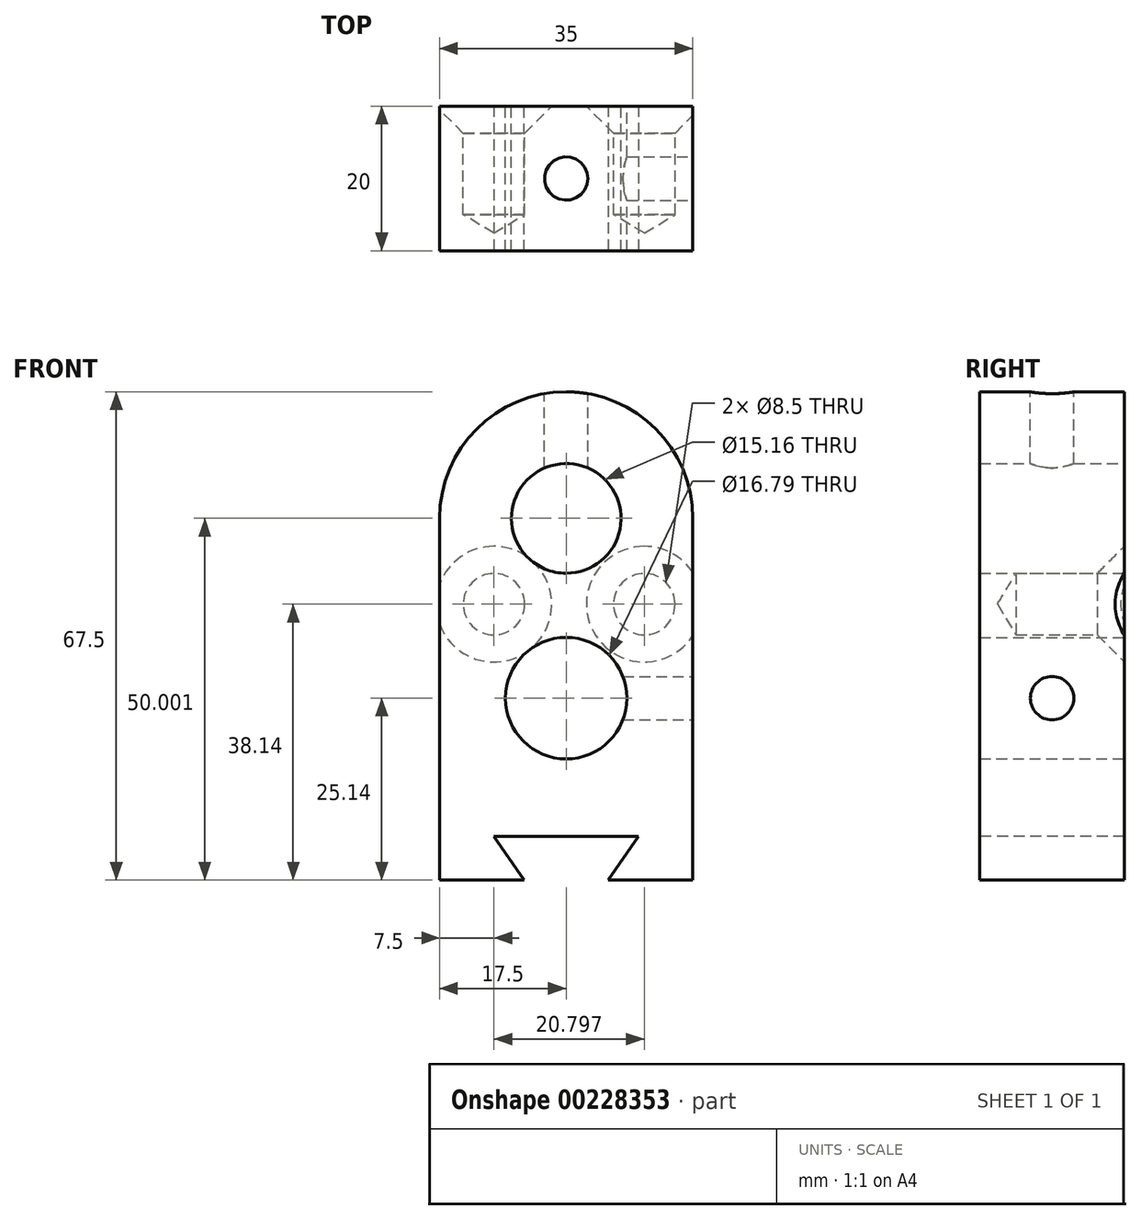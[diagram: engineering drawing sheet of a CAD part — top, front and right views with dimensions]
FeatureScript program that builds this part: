
annotation { "Feature Type Name" : "Feature", "Feature Type Description" : "" }
export const myFeature = defineFeature(function(context is Context, id is Id, definition is map)
    precondition{}
    {
        {
            var Q0;
            Q0=qCreatedBy(makeId("Front.planeOp"),FACE);
            var sketch = newSketch(context, id + "F0", { "sketchPlane" : qUnion([Q0])});
            skLineSegment(sketch, "E0.bottom", {"start": v(-17.5, -25.14) * mm, "end": v(17.5, -25.14) * mm});
            skLineSegment(sketch, "E0.left", {"start": v(-17.5, -25.14) * mm, "end": v(-17.5, 24.86) * mm});
            skLineSegment(sketch, "E0.right", {"start": v(17.5, -25.14) * mm, "end": v(17.5, 24.86) * mm});
            skArc(sketch, "E1", {"start": v(17.5, 24.86) * mm, "mid": v(0, 42.36) * mm, "end": v(-17.5, 24.86) * mm});
            skCircle(sketch, "E2", {"center": v(0, 24.86) * mm, "radius": 7.58 * mm});
            skCircle(sketch, "E3", {"center": v(0, 0) * mm, "radius": 8.4 * mm});
            skSolve(sketch);
        }
        {
            var Q0;
            Q0=makeQuery(id+"F0.imprint","IMPRINT",FACE,{"disambiguationData":[TD([[makeQuery(id+"F0.imprint","IMPRINT",EDGE,{"derivedFrom":sQuery(id+"F0.wireOp",EDGE,"E0.bottom")}),1.0]])]});
            extrude(context, id + "F1", {"entities" : qUnion([Q0]), "depth" : 20 * mm});
        }
        {
            var Q0;
            Q0=makeQuery(id+"F1.opExtrude","CAP_FACE",FACE,{"disambiguationData":[OSD([sQuery(id+"F0.wireOp",EDGE,"E0.bottom"),sQuery(id+"F0.wireOp",EDGE,"E0.left"),sQuery(id+"F0.wireOp",EDGE,"E0.right"),sQuery(id+"F0.wireOp",EDGE,"E1"),sQuery(id+"F0.wireOp",EDGE,"E2"),sQuery(id+"F0.wireOp",EDGE,"E3")])],"isStart":false});
            var sketch = newSketch(context, id + "F2", { "sketchPlane" : qUnion([Q0])});
            skLineSegment(sketch, "E4", {"start": v(0, -26.69) * mm, "end": v(0, -25.14) * mm, "construction": true});
            skLineSegment(sketch, "E5", {"start": v(8.93, -19.1) * mm, "end": v(7.4, -25.14) * mm});
            skLineSegment(sketch, "E6", {"start": v(7.4, -25.14) * mm, "end": v(-6.96, -25.14) * mm});
            skLineSegment(sketch, "E7", {"start": v(-6.96, -25.14) * mm, "end": v(-11.07, -26.69) * mm});
            skLineSegment(sketch, "E8", {"start": v(-11.07, -26.69) * mm, "end": v(8.93, -19.1) * mm});
            skSolve(sketch);
        }
        {
            var Q0;
            {var subQ3=sQuery(id+"F2.wireOp",EDGE,"E5");Q0=makeQuery(id+"F2.imprint","IMPRINT",FACE,{"disambiguationData":[TD([[makeQuery(id+"F2.imprint","IMPRINT",EDGE,{"derivedFrom":subQ3}),1.0]])]});}
            var sketch = newSketch(context, id + "F3", { "sketchPlane" : qUnion([Q0])});
            skLineSegment(sketch, "E9", {"start": v(-5.73, -25.24) * mm, "end": v(-10, -19.14) * mm});
            skLineSegment(sketch, "E10", {"start": v(-10, -19.14) * mm, "end": v(10, -19.14) * mm});
            skLineSegment(sketch, "E11", {"start": v(10, -19.14) * mm, "end": v(5.75, -25.2) * mm});
            skLineSegment(sketch, "E12", {"start": v(-5.73, -25.24) * mm, "end": v(5.75, -25.2) * mm});
            skSolve(sketch);
        }
        {
            var Q0;
            {var subQ0=sQuery(id+"F3.wireOp",EDGE,"E10");var subQ1=sQuery(id+"F3.wireOp",EDGE,"E9");var subQ2=makeQuery(id+"F3.imprint","INTERSECT",VERTEX,{"derivedFrom":[subQ1,subQ0]});Q0=makeQuery(id+"F3.imprint","IMPRINT",FACE,{"disambiguationData":[TD([[makeQuery(id+"F3.imprint","IMPRINT",EDGE,{"disambiguationData":[TD([[subQ2,1.0]])],"derivedFrom":subQ1}),-1.0]])]});}
            var Q1;
            {var subQ0=sQuery(id+"F3.wireOp",EDGE,"E12");Q1=makeQuery(id+"F3.imprint","IMPRINT",FACE,{"disambiguationData":[TD([[makeQuery(id+"F3.imprint","IMPRINT",EDGE,{"derivedFrom":subQ0}),1.0]])]});}
            var Q2;
            {var subQ0=sQuery(id+"F3.wireOp",EDGE,"E11");var subQ1=sQuery(id+"F3.wireOp",EDGE,"E10");var subQ2=makeQuery(id+"F3.imprint","INTERSECT",VERTEX,{"derivedFrom":[subQ1,subQ0]});Q2=makeQuery(id+"F3.imprint","IMPRINT",FACE,{"disambiguationData":[TD([[makeQuery(id+"F3.imprint","IMPRINT",EDGE,{"disambiguationData":[TD([[subQ2,1.0]])],"derivedFrom":subQ1}),-1.0]])]});}
            extrude(context, id + "F4", {"entities" : qUnion([Q0, Q1, Q2]), "operationType" : NewBodyOperationType.REMOVE, "oppositeDirection" : true, "depth" : 25 * mm});
        }
        {
            var Q0;
            Q0=makeQuery(id+"F1.opExtrude","SWEPT_FACE",FACE,{"disambiguationData":[OSD([sQuery(id+"F0.wireOp",EDGE,"E0.right")])]});
            var sketch = newSketch(context, id + "F5", { "sketchPlane" : qUnion([Q0])});
            skLineSegment(sketch, "E13", {"start": v(-10, 24.86) * mm, "end": v(-10, -25.14) * mm, "construction": true});
            skCircle(sketch, "E14", {"center": v(-10, 0) * mm, "radius": 3 * mm});
            skSolve(sketch);
        }
        {
            var Q0;
            Q0=makeQuery(id+"F5.imprint","IMPRINT",FACE,{"disambiguationData":[TD([[makeQuery(id+"F5.imprint","IMPRINT",EDGE,{"derivedFrom":sQuery(id+"F5.wireOp",EDGE,"E14")}),1.0]])]});
            extrude(context, id + "F6", {"entities" : qUnion([Q0]), "operationType" : NewBodyOperationType.REMOVE, "oppositeDirection" : true, "depth" : 10 * mm});
        }
        {
            var Q0;
            Q0=qCreatedBy(makeId("Top.planeOp"),FACE);
            cPlane(context, id + "F7", {"entities" : qUnion([Q0]), "cplaneType" : CPlaneType.OFFSET, "offset" : 67.5 * mm, "width" : 150 * mm, "height" : 150 * mm});
        }
        {
            var Q0;
            Q0=qCreatedBy(id+"F7.planeOp",FACE);
            var sketch = newSketch(context, id + "F8", { "sketchPlane" : qUnion([Q0])});
            skCircle(sketch, "E15", {"center": v(0, -10) * mm, "radius": 3 * mm});
            skSolve(sketch);
        }
        {
            var Q0;
            Q0=makeQuery(id+"F8.imprint","IMPRINT",FACE,{"disambiguationData":[TD([[makeQuery(id+"F8.imprint","IMPRINT",EDGE,{"derivedFrom":sQuery(id+"F8.wireOp",EDGE,"E15")}),1.0]])]});
            extrude(context, id + "F9", {"entities" : qUnion([Q0]), "operationType" : NewBodyOperationType.REMOVE, "oppositeDirection" : true, "depth" : 40 * mm});
        }
        {
            var Q0;
            Q0=makeQuery(id+"F1.opExtrude","CAP_FACE",FACE,{"disambiguationData":[OSD([sQuery(id+"F0.wireOp",EDGE,"E0.bottom"),sQuery(id+"F0.wireOp",EDGE,"E0.left"),sQuery(id+"F0.wireOp",EDGE,"E0.right"),sQuery(id+"F0.wireOp",EDGE,"E1"),sQuery(id+"F0.wireOp",EDGE,"E2"),sQuery(id+"F0.wireOp",EDGE,"E3")])],"isStart":true});
            var sketch = newSketch(context, id + "F10", { "sketchPlane" : qUnion([Q0])});
            skPoint(sketch, "E16", {"position": v(10, 13) * mm});
            skPoint(sketch, "E17", {"position": v(-10.8, 13) * mm});
            skSolve(sketch);
        }
        {
            var Q0;
            Q0=sQuery(id+"F10.wireOp",VERTEX,"E16");
            var Q1;
            Q1=sQuery(id+"F10.wireOp",VERTEX,"E17");
            var Q2;
            Q2=makeQuery(id+"F1.opExtrude","SWEPT_BODY",BODY,{"disambiguationData":[OSD([sQuery(id+"F0.wireOp",EDGE,"E0.bottom"),sQuery(id+"F0.wireOp",EDGE,"E0.left"),sQuery(id+"F0.wireOp",EDGE,"E0.right"),sQuery(id+"F0.wireOp",EDGE,"E1"),sQuery(id+"F0.wireOp",EDGE,"E2"),sQuery(id+"F0.wireOp",EDGE,"E3")])]});
            hole(context, id + "F11", {"style" : HoleStyle.C_SINK, "endStyle" : HoleEndStyle.BLIND, "holeDiameter" : 8.5 * mm, "cSinkDiameter" : 16 * mm, "cSinkAngle" : 90 * degree, "holeDepth" : 15 * mm, "startFromSketch" : true, "locations" : qUnion([Q0, Q1]), "scope" : qUnion([Q2])});
        }
    });
